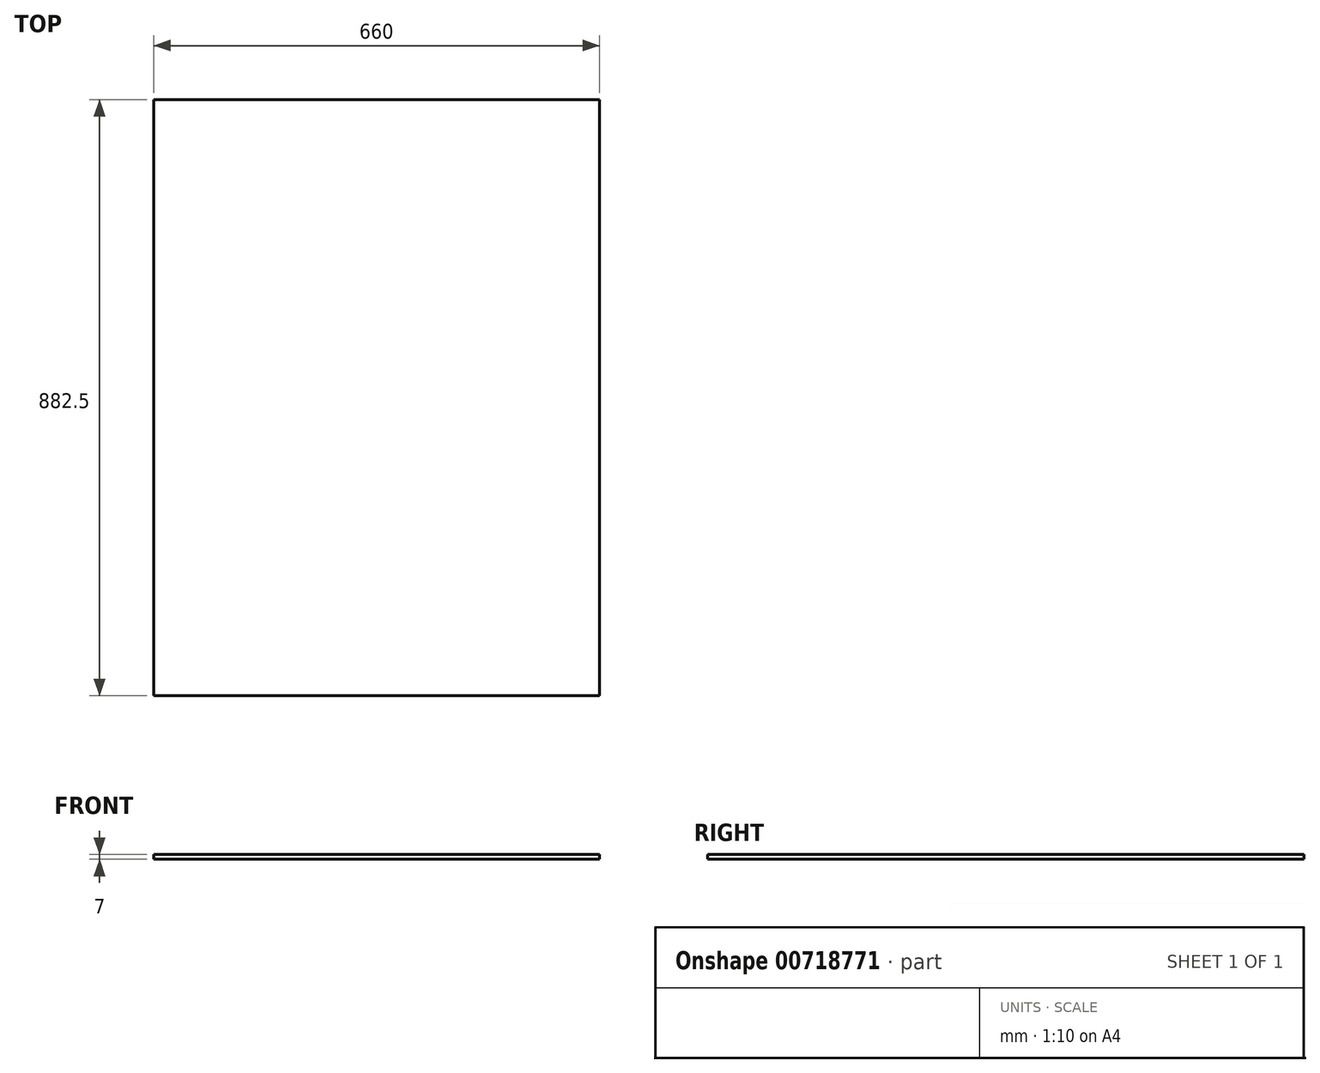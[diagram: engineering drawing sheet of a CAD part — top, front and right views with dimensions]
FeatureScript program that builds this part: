
annotation { "Feature Type Name" : "Feature", "Feature Type Description" : "" }
export const myFeature = defineFeature(function(context is Context, id is Id, definition is map)
    precondition{}
    {
        {
            var Q0;
            Q0=qCreatedBy(makeId("Top.planeOp"),FACE);
            var sketch = newSketch(context, id + "F0", { "sketchPlane" : qUnion([Q0])});
            skLineSegment(sketch, "E0.bottom", {"start": v(0, 0) * mm, "end": v(660, 0) * mm});
            skLineSegment(sketch, "E0.top", {"start": v(0, 882.5) * mm, "end": v(660, 882.5) * mm});
            skLineSegment(sketch, "E0.left", {"start": v(0, 0) * mm, "end": v(0, 882.5) * mm});
            skLineSegment(sketch, "E0.right", {"start": v(660, 0) * mm, "end": v(660, 882.5) * mm});
            skSolve(sketch);
        }
        {
            var Q0;
            Q0 = qSketchRegion(id + "F0", true);
            extrude(context, id + "F1", {"entities" : qUnion([Q0]), "depth" : 7 * mm, "offsetDistance" : 25.4 * mm});
        }
    });
